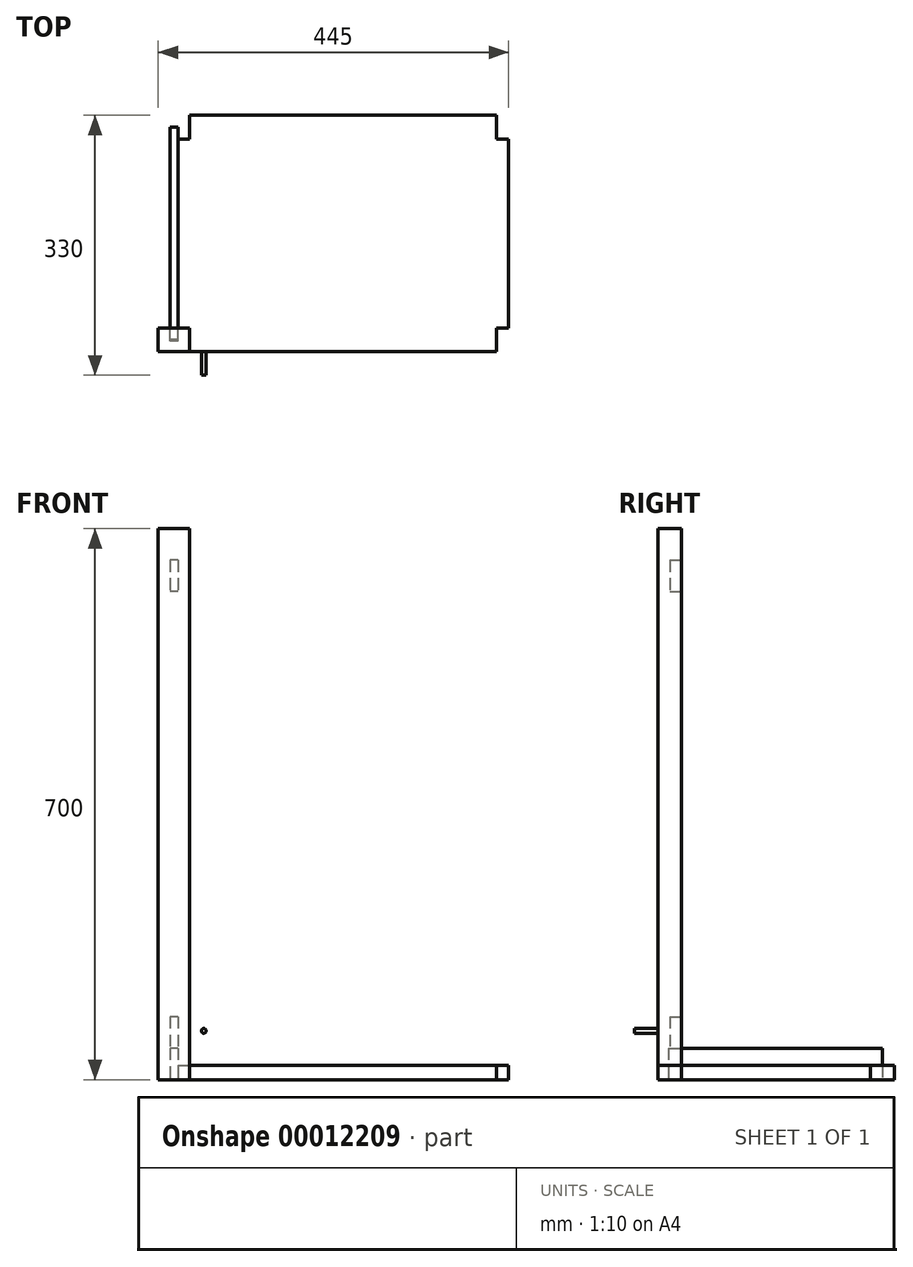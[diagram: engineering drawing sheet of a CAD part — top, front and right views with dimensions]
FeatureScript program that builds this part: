
annotation { "Feature Type Name" : "Feature", "Feature Type Description" : "" }
export const myFeature = defineFeature(function(context is Context, id is Id, definition is map)
    precondition{}
    {
        {
            var Q0;
            Q0=qCreatedBy(makeId("Top.planeOp"),FACE);
            var sketch = newSketch(context, id + "F0", { "sketchPlane" : qUnion([Q0])});
            skLineSegment(sketch, "E0", {"start": v(0, 30) * mm, "end": v(15, 30) * mm});
            skLineSegment(sketch, "E1", {"start": v(15, 30) * mm, "end": v(15, 0) * mm});
            skLineSegment(sketch, "E2", {"start": v(15, 0) * mm, "end": v(405, 0) * mm});
            skLineSegment(sketch, "E3", {"start": v(405, 0) * mm, "end": v(405, 30) * mm});
            skLineSegment(sketch, "E4", {"start": v(405, 30) * mm, "end": v(420, 30) * mm});
            skLineSegment(sketch, "E5", {"start": v(420, 30) * mm, "end": v(420, 270) * mm});
            skLineSegment(sketch, "E6", {"start": v(420, 270) * mm, "end": v(405, 270) * mm});
            skLineSegment(sketch, "E7", {"start": v(405, 270) * mm, "end": v(405, 300) * mm});
            skLineSegment(sketch, "E8", {"start": v(405, 300) * mm, "end": v(15, 300) * mm});
            skLineSegment(sketch, "E9", {"start": v(15, 300) * mm, "end": v(15, 270) * mm});
            skLineSegment(sketch, "E10", {"start": v(15, 270) * mm, "end": v(0, 270) * mm});
            skLineSegment(sketch, "E11", {"start": v(0, 270) * mm, "end": v(0, 30) * mm});
            skSolve(sketch);
        }
        {
            var Q0;
            Q0 = qSketchRegion(id + "F0", true);
            extrude(context, id + "F1", {"entities" : qUnion([Q0]), "depth" : 18 * mm});
        }
        {
            var Q0;
            Q0=qCreatedBy(makeId("Top.planeOp"),FACE);
            var sketch = newSketch(context, id + "F2", { "sketchPlane" : qUnion([Q0])});
            skLineSegment(sketch, "E12", {"start": v(15, 0) * mm, "end": v(-25, 0) * mm});
            skLineSegment(sketch, "E13", {"start": v(-25, 0) * mm, "end": v(-25, 30) * mm});
            skLineSegment(sketch, "E14", {"start": v(-25, 30) * mm, "end": v(15, 30) * mm});
            skLineSegment(sketch, "E15", {"start": v(15, 30) * mm, "end": v(15, 0) * mm});
            skSolve(sketch);
        }
        {
            var Q0;
            Q0 = qSketchRegion(id + "F2", true);
            extrude(context, id + "F3", {"entities" : qUnion([Q0]), "depth" : 700 * mm});
        }
        {
            var Q0;
            Q0=qCreatedBy(makeId("Top.planeOp"),FACE);
            var sketch = newSketch(context, id + "F4", { "sketchPlane" : qUnion([Q0])});
            skLineSegment(sketch, "E16.bottom", {"start": v(0, 13.51) * mm, "end": v(-10, 13.51) * mm});
            skLineSegment(sketch, "E16.top", {"start": v(0, 285) * mm, "end": v(-10, 285) * mm});
            skLineSegment(sketch, "E16.left", {"start": v(0, 13.51) * mm, "end": v(0, 285) * mm});
            skLineSegment(sketch, "E16.right", {"start": v(-10, 13.51) * mm, "end": v(-10, 285) * mm});
            skSolve(sketch);
        }
        {
            var Q0;
            Q0 = qSketchRegion(id + "F4", true);
            extrude(context, id + "F5", {"entities" : qUnion([Q0]), "depth" : 40 * mm});
        }
        {
            var Q0;
            Q0=qCreatedBy(makeId("Front.planeOp"),FACE);
            var sketch = newSketch(context, id + "F6", { "sketchPlane" : qUnion([Q0])});
            skCircle(sketch, "E17", {"center": v(32.98, 61.99) * mm, "radius": 3 * mm});
            skSolve(sketch);
        }
        {
            var Q0;
            Q0 = qSketchRegion(id + "F6", true);
            extrude(context, id + "F7", {"entities" : qUnion([Q0]), "depth" : 30 * mm});
        }
        {
            var Q0;
            Q0=makeQuery(id+"F3.opExtrude","SWEPT_FACE",FACE,{"disambiguationData":[OSD([sQuery(id+"F2.wireOp",EDGE,"E14")])]});
            var sketch = newSketch(context, id + "F8", { "sketchPlane" : qUnion([Q0])});
            skLineSegment(sketch, "E18.bottom", {"start": v(0, 660) * mm, "end": v(10, 660) * mm});
            skLineSegment(sketch, "E18.top", {"start": v(0, 620) * mm, "end": v(10, 620) * mm});
            skLineSegment(sketch, "E18.left", {"start": v(0, 660) * mm, "end": v(0, 620) * mm});
            skLineSegment(sketch, "E18.right", {"start": v(10, 660) * mm, "end": v(10, 620) * mm});
            skLineSegment(sketch, "E19.left", {"start": v(0, 80) * mm, "end": v(0, 40) * mm});
            skLineSegment(sketch, "E19.top", {"start": v(0, 40) * mm, "end": v(10, 40) * mm});
            skLineSegment(sketch, "E19.right", {"start": v(10, 80) * mm, "end": v(10, 40) * mm});
            skLineSegment(sketch, "E19.bottom", {"start": v(0, 80) * mm, "end": v(10, 80) * mm});
            skSolve(sketch);
        }
        {
            var Q0;
            Q0=makeQuery(id+"F8.imprint","IMPRINT",FACE,{"disambiguationData":[TD([[makeQuery(id+"F8.imprint","IMPRINT",EDGE,{"derivedFrom":sQuery(id+"F8.wireOp",EDGE,"E18.bottom")}),-1.0]])]});
            var Q1;
            Q1=makeQuery(id+"F8.imprint","IMPRINT",FACE,{"disambiguationData":[TD([[makeQuery(id+"F8.imprint","IMPRINT",EDGE,{"derivedFrom":sQuery(id+"F8.wireOp",EDGE,"E19.left")}),1.0]])]});
            extrude(context, id + "F9", {"entities" : qUnion([Q0, Q1]), "operationType" : NewBodyOperationType.REMOVE, "oppositeDirection" : true, "depth" : 15 * mm});
        }
    });
